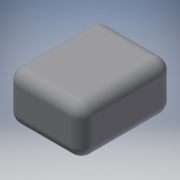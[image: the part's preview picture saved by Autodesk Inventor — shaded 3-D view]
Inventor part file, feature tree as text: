
AUTODESK INVENTOR PART (.ipt)
format: ipt  version: 2018 (Build 220112000, 112)  size: 122,880 bytes
history: native  units: in
note: dims shown in document units (in); Inventor stores cm internally (conversion verified against a paired STEP export)
features: extrude x1, fillet x1, sketch x1
ambient origin geometry x8: Origin, YZ Plane, XZ Plane, XY Plane, X Axis, Y Axis, Z Axis, Center Point
bodies: Solid1 (feature_tree)
feature tree (3):
  extrude  "Extrusion1"  Depth=0.4in
  fillet  "Fillet1"  Radius=0.21in
  sketch  "Sketch1"  dims[d0=0.325in d1=0.4in d2=0.21in d3=0.0in d4=0.05in]
